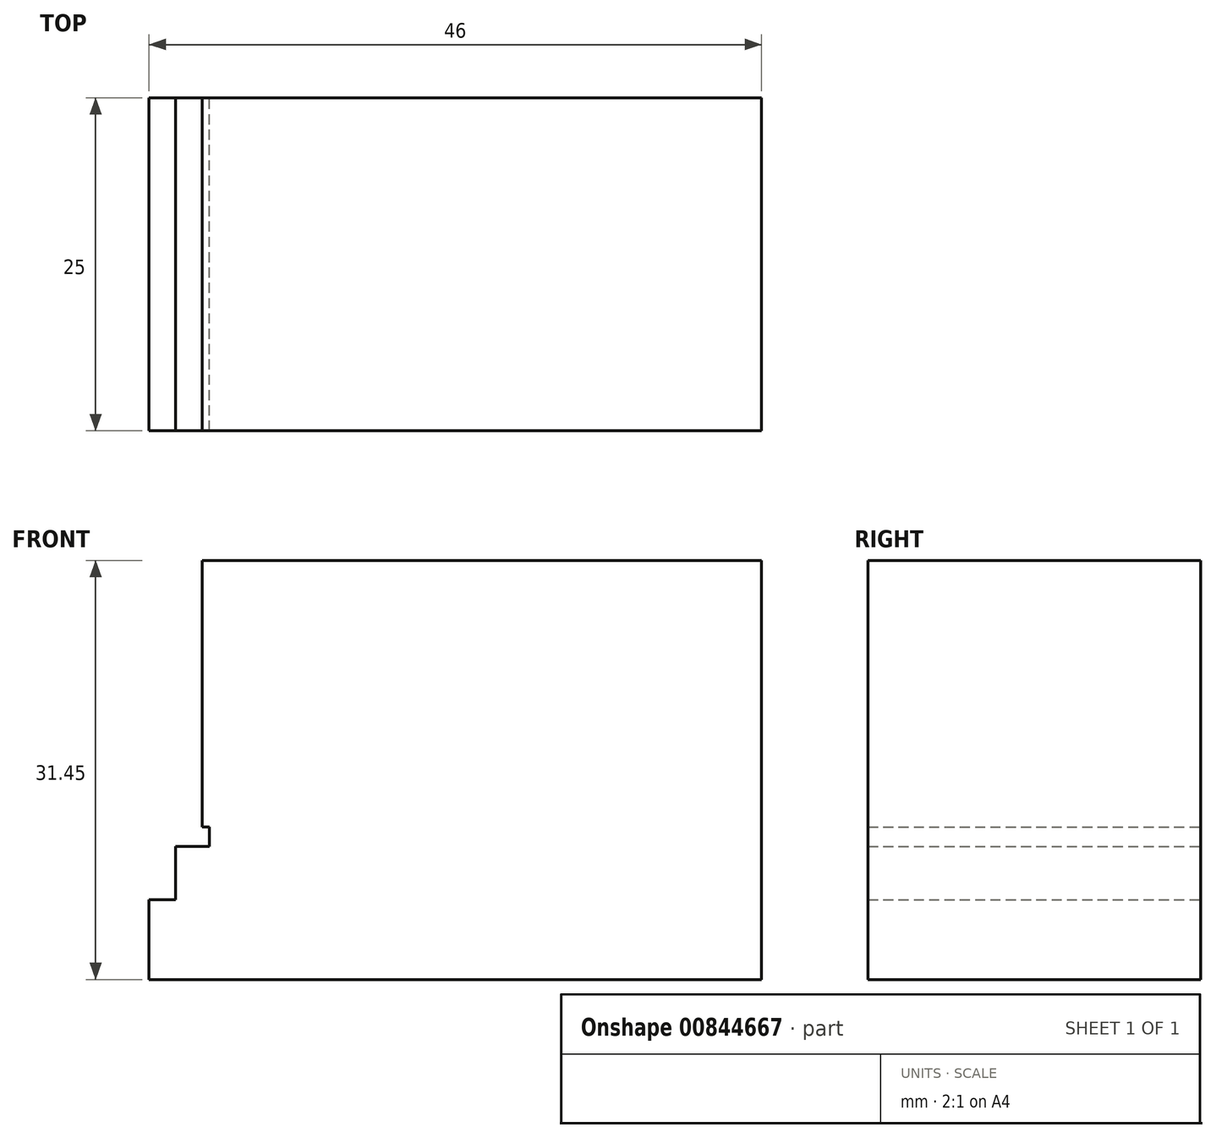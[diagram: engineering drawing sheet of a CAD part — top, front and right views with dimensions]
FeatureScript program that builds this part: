
annotation { "Feature Type Name" : "Feature", "Feature Type Description" : "" }
export const myFeature = defineFeature(function(context is Context, id is Id, definition is map)
    precondition{}
    {
        {
            var Q0;
            Q0=qCreatedBy(makeId("Front.planeOp"),FACE);
            var sketch = newSketch(context, id + "F0", { "sketchPlane" : qUnion([Q0])});
            skLineSegment(sketch, "E0.bottom", {"start": v(0, 0) * mm, "end": v(-41.45, 0) * mm});
            skLineSegment(sketch, "E0.top", {"start": v(0, 1.45) * mm, "end": v(-41.45, 1.45) * mm});
            skLineSegment(sketch, "E0.left", {"start": v(0, 0) * mm, "end": v(0, 1.45) * mm});
            skLineSegment(sketch, "E0.right", {"start": v(-41.45, 0) * mm, "end": v(-41.45, 1.45) * mm});
            skLineSegment(sketch, "E1.bottom", {"start": v(0, 0) * mm, "end": v(-44, 0) * mm});
            skLineSegment(sketch, "E1.top", {"start": v(0, -4) * mm, "end": v(-44, -4) * mm});
            skLineSegment(sketch, "E1.left", {"start": v(0, 0) * mm, "end": v(0, -4) * mm});
            skLineSegment(sketch, "E1.right", {"start": v(-44, 0) * mm, "end": v(-44, -4) * mm});
            skLineSegment(sketch, "E2.bottom", {"start": v(0, 1.45) * mm, "end": v(-42, 1.45) * mm});
            skLineSegment(sketch, "E2.top", {"start": v(0, 21.45) * mm, "end": v(-42, 21.45) * mm});
            skLineSegment(sketch, "E2.left", {"start": v(0, 1.45) * mm, "end": v(0, 21.45) * mm});
            skLineSegment(sketch, "E2.right", {"start": v(-42, 1.45) * mm, "end": v(-42, 21.45) * mm});
            skLineSegment(sketch, "E3.bottom", {"start": v(0, -4) * mm, "end": v(-46, -4) * mm});
            skLineSegment(sketch, "E3.top", {"start": v(0, -10) * mm, "end": v(-46, -10) * mm});
            skLineSegment(sketch, "E3.left", {"start": v(0, -4) * mm, "end": v(0, -10) * mm});
            skLineSegment(sketch, "E3.right", {"start": v(-46, -4) * mm, "end": v(-46, -10) * mm});
            skSolve(sketch);
        }
        {
            var Q0;
            Q0 = qSketchRegion(id + "F0", true);
            extrude(context, id + "F1", {"entities" : qUnion([Q0]), "depth" : 25 * mm, "offsetDistance" : 25 * mm});
        }
    });
